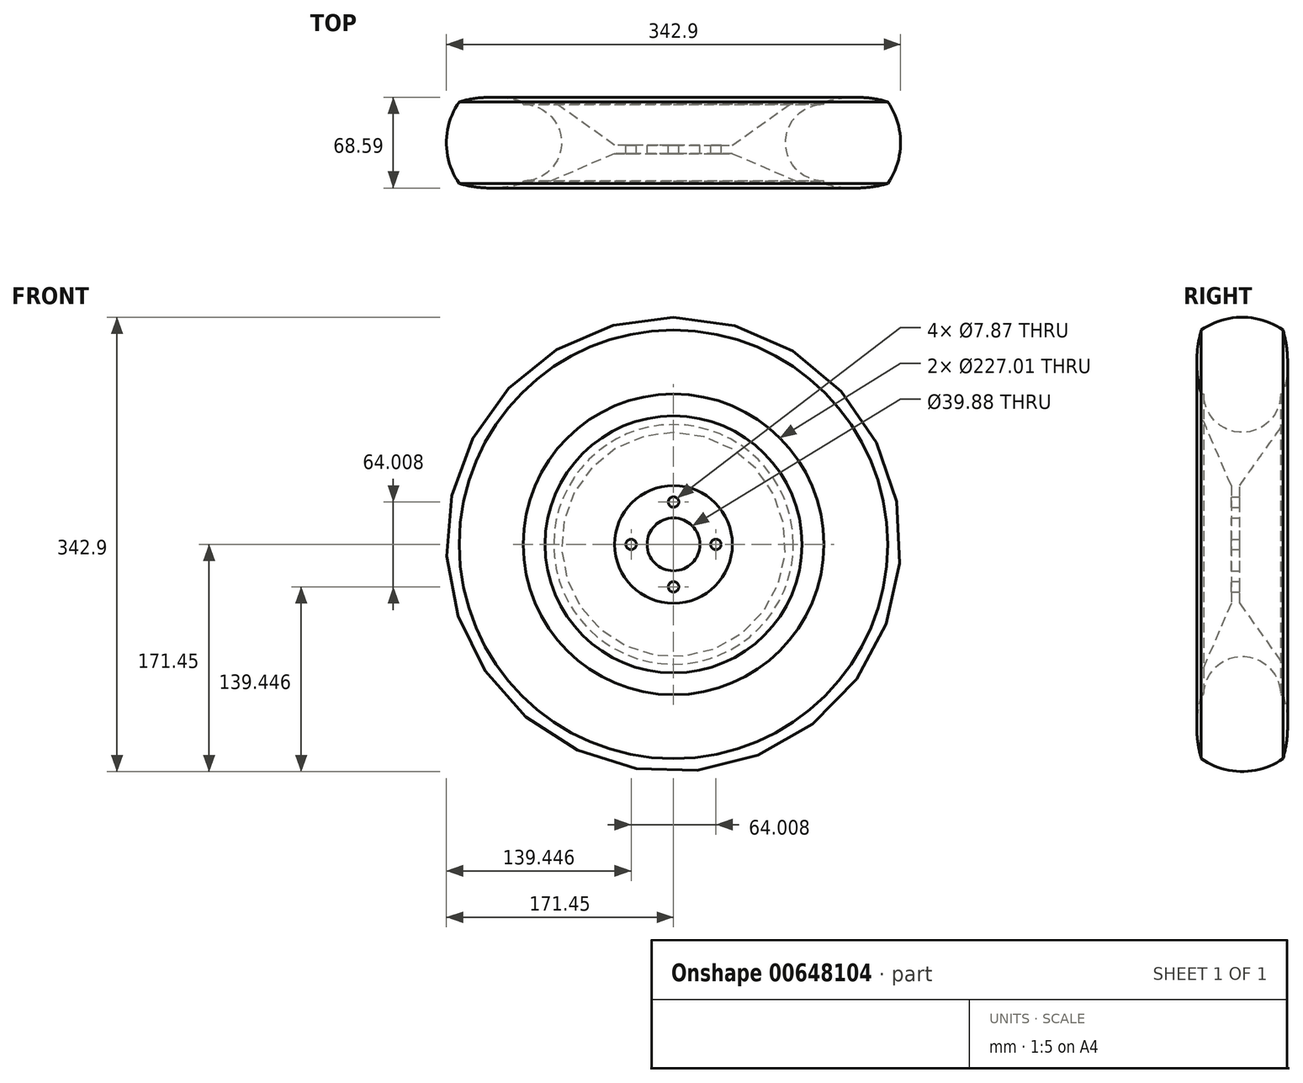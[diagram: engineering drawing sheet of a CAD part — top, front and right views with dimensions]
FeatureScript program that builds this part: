
annotation { "Feature Type Name" : "Feature", "Feature Type Description" : "" }
export const myFeature = defineFeature(function(context is Context, id is Id, definition is map)
    precondition{}
    {
        {
            var Q0;
            Q0=qCreatedBy(makeId("Front.planeOp"),FACE);
            var sketch = newSketch(context, id + "F0", { "sketchPlane" : qUnion([Q0])});
            skCircle(sketch, "E0", {"center": v(0, 0) * mm, "radius": 19.94 * mm});
            skCircle(sketch, "E1", {"center": v(0, 0) * mm, "radius": 44.45 * mm});
            skCircle(sketch, "E2", {"center": v(0, 32) * mm, "radius": 3.94 * mm});
            skCircle(sketch, "E3.1.0", {"center": v(-32, 0) * mm, "radius": 3.94 * mm});
            skCircle(sketch, "E3.2.0", {"center": v(0, -32) * mm, "radius": 3.94 * mm});
            skCircle(sketch, "E3.3.0", {"center": v(32, 0) * mm, "radius": 3.94 * mm});
            skSolve(sketch);
        }
        {
            var Q0;
            Q0 = qSketchRegion(id + "F0", true);
            extrude(context, id + "F1", {"entities" : qUnion([Q0]), "depth" : 6.35 * mm, "offsetDistance" : 25.4 * mm});
        }
        {
            var Q0;
            Q0=qCreatedBy(makeId("Top.planeOp"),FACE);
            var sketch = newSketch(context, id + "F2", { "sketchPlane" : qUnion([Q0])});
            skLineSegment(sketch, "E4", {"start": v(-44.45, -6.35) * mm, "end": v(-97, -28.96) * mm});
            skLineSegment(sketch, "E5", {"start": v(-90.45, 32.77) * mm, "end": v(-44.45, 0) * mm});
            skLineSegment(sketch, "E6", {"start": v(-44.45, -6.35) * mm, "end": v(-44.45, 0) * mm});
            skLineSegment(sketch, "E7", {"start": v(-97, -28.96) * mm, "end": v(-113.5, -28.96) * mm});
            skLineSegment(sketch, "E8", {"start": v(-113.5, -28.96) * mm, "end": v(-113.5, -27.05) * mm});
            skLineSegment(sketch, "E9", {"start": v(-113.5, 32.77) * mm, "end": v(-90.45, 32.77) * mm});
            skArc(sketch, "E10", {"start": v(-113.5, -27.05) * mm, "mid": v(-84.55, 1.9) * mm, "end": v(-113.5, 30.86) * mm});
            skLineSegment(sketch, "E11.trimOffspring", {"start": v(-113.5, 30.86) * mm, "end": v(-113.5, 32.77) * mm});
            skLineSegment(sketch, "E12", {"start": v(0, 0) * mm, "end": v(0, -21.36) * mm, "construction": true});
            skSolve(sketch);
        }
        {
            var Q0;
            Q0 = qSketchRegion(id + "F2", true);
            var Q1;
            Q1=sQuery(id+"F2.wireOp",EDGE,"E12");
            revolve(context, id + "F3", {"operationType" : NewBodyOperationType.ADD, "entities" : qUnion([Q0]), "axis" : qUnion([Q1]), "revolveType" : RevolveType.FULL});
        }
        {
            var Q0;
            Q0=qCreatedBy(makeId("Right.planeOp"),FACE);
            var sketch = newSketch(context, id + "F4", { "sketchPlane" : qUnion([Q0])});
            skLineSegment(sketch, "E13", {"start": v(0, 0) * mm, "end": v(-38.04, 0) * mm, "construction": true});
            skArc(sketch, "E14", {"start": v(-27.05, 113.5) * mm, "mid": v(1.9, 84.55) * mm, "end": v(30.86, 113.5) * mm});
            skLineSegment(sketch, "E15", {"start": v(30.86, 113.5) * mm, "end": v(32.77, 113.5) * mm});
            skLineSegment(sketch, "E16", {"start": v(-28.96, 113.5) * mm, "end": v(-27.05, 113.5) * mm});
            skArc(sketch, "E17", {"start": v(32.77, 113.5) * mm, "mid": v(36.2, 137.64) * mm, "end": v(32.77, 161.77) * mm});
            skLineSegment(sketch, "E18", {"start": v(1.9, 84.55) * mm, "end": v(1.9, 108.78) * mm, "construction": true});
            skArc(sketch, "E19.MirrorCS", {"start": v(-28.96, 113.5) * mm, "mid": v(-32.39, 137.64) * mm, "end": v(-28.96, 161.77) * mm});
            skArc(sketch, "E20", {"start": v(32.77, 161.77) * mm, "mid": v(1.9, 171.45) * mm, "end": v(-28.96, 161.77) * mm});
            skSolve(sketch);
        }
        {
            var Q0;
            Q0 = qSketchRegion(id + "F4", true);
            var Q1;
            Q1=sQuery(id+"F4.wireOp",EDGE,"E13");
            revolve(context, id + "F5", {"entities" : qUnion([Q0]), "axis" : qUnion([Q1]), "revolveType" : RevolveType.FULL});
        }
    });
